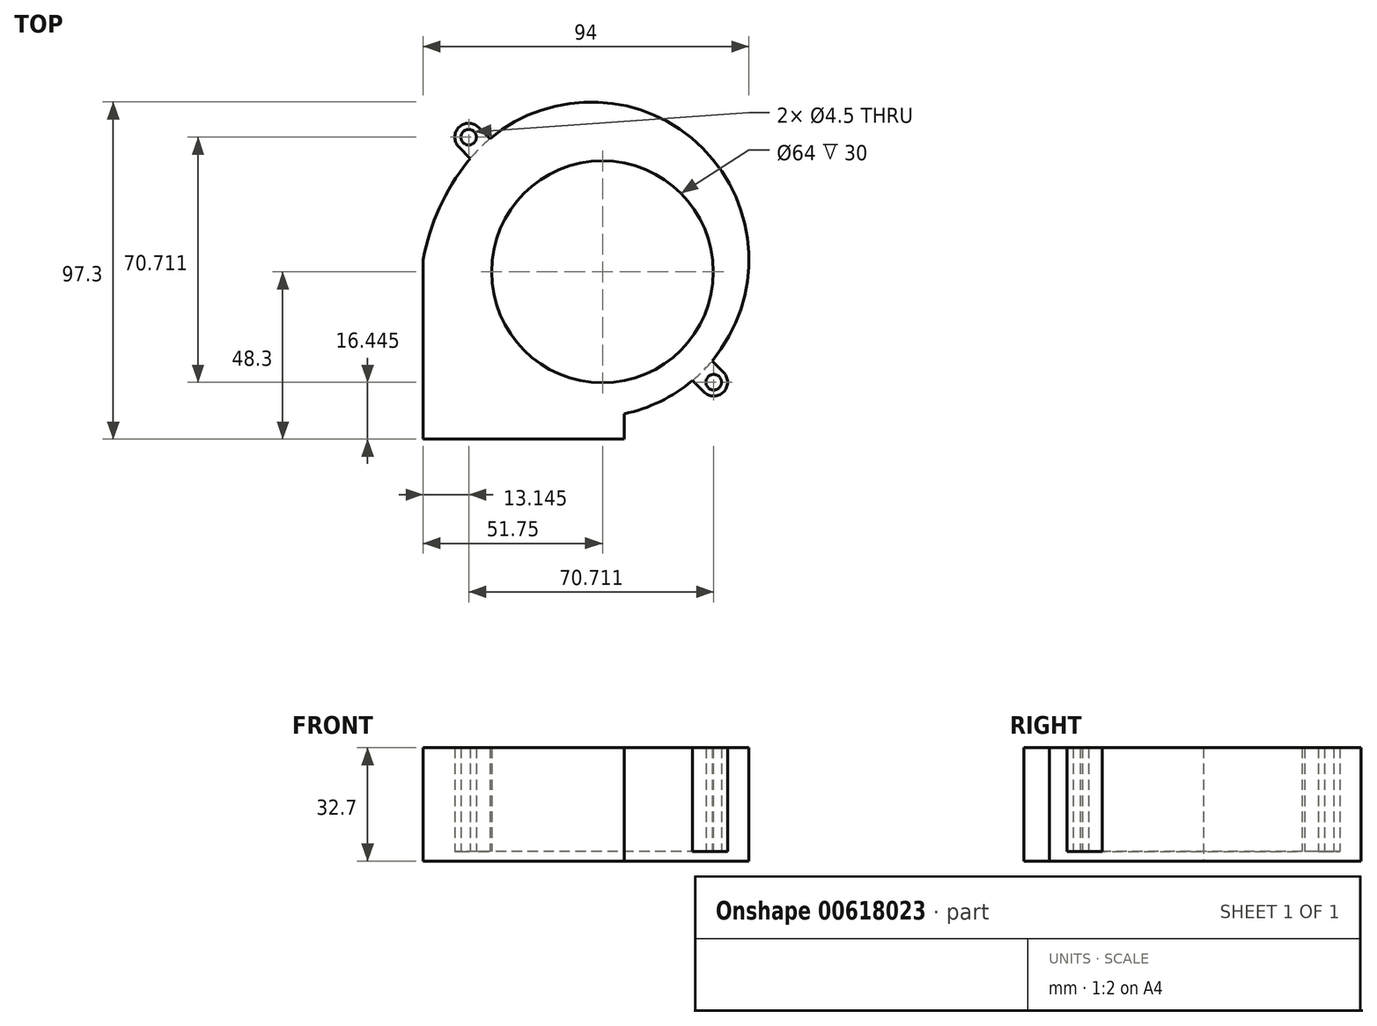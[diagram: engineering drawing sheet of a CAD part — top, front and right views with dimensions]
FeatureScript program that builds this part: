
annotation { "Feature Type Name" : "Feature", "Feature Type Description" : "" }
export const myFeature = defineFeature(function(context is Context, id is Id, definition is map)
    precondition{}
    {
        {
            var Q0;
            Q0=qCreatedBy(makeId("Top.planeOp"),FACE);
            var sketch = newSketch(context, id + "F0", { "sketchPlane" : qUnion([Q0])});
            skCircle(sketch, "E0", {"center": v(3.25, -3.5) * mm, "radius": 32 * mm});
            skPoint(sketch, "E1.endSnap0", {"position": v(31.88, 45.5) * mm});
            skLineSegment(sketch, "E2", {"start": v(-48.5, -51.8) * mm, "end": v(9.5, -51.8) * mm});
            skArc(sketch, "E3", {"start": v(-35.63, 28.3) * mm, "mid": v(38.67, 23.97) * mm, "end": v(9.5, -44.5) * mm});
            skLineSegment(sketch, "E4", {"start": v(-48.5, -51.8) * mm, "end": v(-48.5, 0) * mm});
            skArc(sketch, "E5", {"start": v(-35.63, 28.3) * mm, "mid": v(-43.8, 14.94) * mm, "end": v(-48.5, 0) * mm});
            skLineSegment(sketch, "E6", {"start": v(9.5, -44.5) * mm, "end": v(9.5, -51.8) * mm});
            skLineSegment(sketch, "E7", {"start": v(-32.53, 38.18) * mm, "end": v(-29.22, 34.88) * mm});
            skLineSegment(sketch, "E8", {"start": v(-38.18, 32.53) * mm, "end": v(-34.88, 29.22) * mm});
            skArc(sketch, "E9", {"start": v(-32.53, 38.18) * mm, "mid": v(-38.18, 38.18) * mm, "end": v(-38.18, 32.53) * mm});
            skLineSegment(sketch, "E10", {"start": v(32.53, -38.18) * mm, "end": v(29.22, -34.88) * mm});
            skLineSegment(sketch, "E11", {"start": v(38.18, -32.53) * mm, "end": v(34.88, -29.22) * mm});
            skArc(sketch, "E12", {"start": v(38.18, -32.53) * mm, "mid": v(38.18, -38.18) * mm, "end": v(32.53, -38.18) * mm});
            skCircle(sketch, "E13", {"center": v(-35.36, 35.36) * mm, "radius": 2.25 * mm});
            skCircle(sketch, "E14", {"center": v(35.36, -35.36) * mm, "radius": 2.25 * mm});
            skSolve(sketch);
        }
        {
            var Q0;
            Q0 = qSketchRegion(id + "F0", true);
            extrude(context, id + "F1", {"entities" : qUnion([Q0]), "depth" : 30 * mm, "offsetDistance" : 25 * mm});
        }
        {
            var Q0;
            Q0=makeQuery(id+"F0.imprint","IMPRINT",FACE,{"disambiguationData":[TD([[makeQuery(id+"F0.imprint","IMPRINT",EDGE,{"derivedFrom":sQuery(id+"F0.wireOp",EDGE,"E0")}),1.0]])]});
            var Q1;
            Q1=makeQuery(id+"F0.imprint","IMPRINT",FACE,{"disambiguationData":[TD([[makeQuery(id+"F0.imprint","IMPRINT",EDGE,{"derivedFrom":sQuery(id+"F0.wireOp",EDGE,"E0")}),-1.0]])]});
            extrude(context, id + "F2", {"entities" : qUnion([Q0, Q1]), "operationType" : NewBodyOperationType.ADD, "oppositeDirection" : true, "depth" : 2.7 * mm, "offsetDistance" : 25 * mm});
        }
    });
